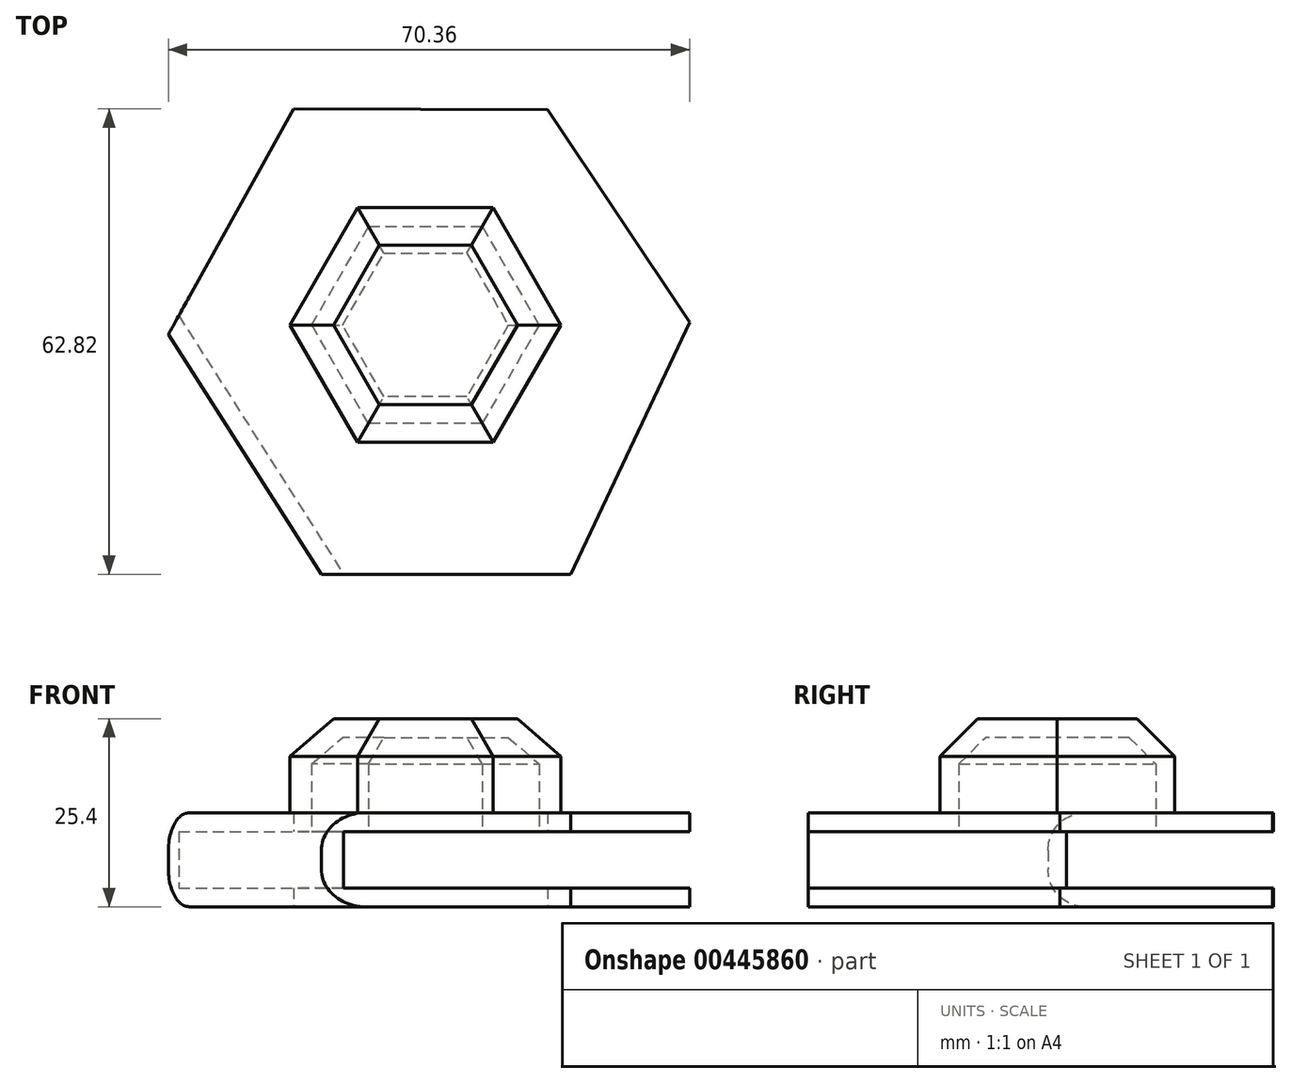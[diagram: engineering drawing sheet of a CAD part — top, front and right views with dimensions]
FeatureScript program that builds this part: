
annotation { "Feature Type Name" : "Feature", "Feature Type Description" : "" }
export const myFeature = defineFeature(function(context is Context, id is Id, definition is map)
    precondition{}
    {
        {
            var Q0;
            Q0=qCreatedBy(makeId("Top.planeOp"),FACE);
            var sketch = newSketch(context, id + "F0", { "sketchPlane" : qUnion([Q0])});
            skCircle(sketch, "E0.cCircle", {"center": v(-11.56, 13.08) * mm, "radius": 15.31 * mm, "construction": true});
            skLineSegment(sketch, "E0.0", {"start": v(-20.05, -2.43) * mm, "end": v(-29.24, 12.67) * mm});
            skLineSegment(sketch, "E0.1", {"start": v(-29.24, 12.67) * mm, "end": v(-20.76, 28.19) * mm});
            skLineSegment(sketch, "E0.2", {"start": v(-20.76, 28.19) * mm, "end": v(-3.08, 28.6) * mm});
            skLineSegment(sketch, "E0.3", {"start": v(-3.08, 28.6) * mm, "end": v(6.11, 13.5) * mm});
            skLineSegment(sketch, "E0.4", {"start": v(6.11, 13.5) * mm, "end": v(-2.37, -2.02) * mm});
            skLineSegment(sketch, "E0.5", {"start": v(-2.37, -2.02) * mm, "end": v(-20.05, -2.43) * mm});
            skPoint(sketch, "E0.0.midPoint", {"position": v(-24.65, 5.12) * mm});
            skLineSegment(sketch, "E1", {"start": v(-2.37, -2.02) * mm, "end": v(7.82, -20.12) * mm});
            skLineSegment(sketch, "E2", {"start": v(7.82, -20.12) * mm, "end": v(-25.85, -20.12) * mm});
            skLineSegment(sketch, "E3", {"start": v(-20.05, -2.43) * mm, "end": v(-25.85, -20.12) * mm});
            skLineSegment(sketch, "E4", {"start": v(6.11, 13.5) * mm, "end": v(23.86, 13.9) * mm});
            skLineSegment(sketch, "E5", {"start": v(23.86, 13.9) * mm, "end": v(7.82, -20.12) * mm});
            skPoint(sketch, "E6.endSnap0", {"position": v(1.52, 21.04) * mm});
            skLineSegment(sketch, "E7", {"start": v(-20.76, 28.19) * mm, "end": v(-29.6, 42.7) * mm});
            skLineSegment(sketch, "E8", {"start": v(-29.24, 12.67) * mm, "end": v(-46.5, 12.27) * mm});
            skLineSegment(sketch, "E9", {"start": v(-46.5, 12.27) * mm, "end": v(-29.6, 42.7) * mm});
            skLineSegment(sketch, "E10", {"start": v(-46.5, 12.27) * mm, "end": v(-25.85, -20.12) * mm});
            skPoint(sketch, "E11.end.orphan", {"position": v(1.52, 46.64) * mm});
            skLineSegment(sketch, "E12", {"start": v(-3.08, 28.6) * mm, "end": v(4.68, 42.57) * mm});
            skLineSegment(sketch, "E13", {"start": v(4.68, 42.57) * mm, "end": v(23.86, 13.9) * mm});
            skLineSegment(sketch, "E14", {"start": v(4.68, 42.57) * mm, "end": v(-29.6, 42.7) * mm});
            skSolve(sketch);
        }
        {
            var Q0;
            Q0=makeQuery(id+"F0.imprint","IMPRINT",FACE,{"disambiguationData":[TD([[makeQuery(id+"F0.imprint","IMPRINT",EDGE,{"derivedFrom":sQuery(id+"F0.wireOp",EDGE,"E0.2")}),1.0]])]});
            var Q1;
            Q1=makeQuery(id+"F0.imprint","IMPRINT",FACE,{"disambiguationData":[TD([[makeQuery(id+"F0.imprint","IMPRINT",EDGE,{"derivedFrom":sQuery(id+"F0.wireOp",EDGE,"E0.3")}),1.0]])]});
            var Q2;
            Q2=makeQuery(id+"F0.imprint","IMPRINT",FACE,{"disambiguationData":[TD([[makeQuery(id+"F0.imprint","IMPRINT",EDGE,{"derivedFrom":sQuery(id+"F0.wireOp",EDGE,"E0.4")}),1.0]])]});
            var Q3;
            Q3=makeQuery(id+"F0.imprint","IMPRINT",FACE,{"disambiguationData":[TD([[makeQuery(id+"F0.imprint","IMPRINT",EDGE,{"derivedFrom":sQuery(id+"F0.wireOp",EDGE,"E0.5")}),1.0]])]});
            var Q4;
            Q4=makeQuery(id+"F0.imprint","IMPRINT",FACE,{"disambiguationData":[TD([[makeQuery(id+"F0.imprint","IMPRINT",EDGE,{"derivedFrom":sQuery(id+"F0.wireOp",EDGE,"E0.0")}),1.0]])]});
            var Q5;
            Q5=makeQuery(id+"F0.imprint","IMPRINT",FACE,{"disambiguationData":[TD([[makeQuery(id+"F0.imprint","IMPRINT",EDGE,{"derivedFrom":sQuery(id+"F0.wireOp",EDGE,"E0.1")}),1.0]])]});
            var Q6;
            Q6=makeQuery(id+"F0.imprint","IMPRINT",FACE,{"disambiguationData":[TD([[makeQuery(id+"F0.imprint","IMPRINT",EDGE,{"derivedFrom":sQuery(id+"F0.wireOp",EDGE,"E0.0")}),-1.0]])]});
            extrude(context, id + "F1", {"entities" : qUnion([Q0, Q1, Q2, Q3, Q4, Q5, Q6]), "depth" : 12.7 * mm});
        }
        {
            var Q0;
            Q0=makeQuery(id+"F1.opExtrude","CAP_FACE",FACE,{"disambiguationData":[OSD([sQuery(id+"F0.wireOp",EDGE,"E2"),sQuery(id+"F0.wireOp",EDGE,"E5"),sQuery(id+"F0.wireOp",EDGE,"E9"),sQuery(id+"F0.wireOp",EDGE,"E10"),sQuery(id+"F0.wireOp",EDGE,"E13"),sQuery(id+"F0.wireOp",EDGE,"E14")])],"isStart":false});
            var sketch = newSketch(context, id + "F2", { "sketchPlane" : qUnion([Q0])});
            skCircle(sketch, "E15.cCircle", {"center": v(-11.8, 13.53) * mm, "radius": 15.83 * mm, "construction": true});
            skLineSegment(sketch, "E15.0", {"start": v(-2.66, -2.3) * mm, "end": v(-20.94, -2.3) * mm});
            skLineSegment(sketch, "E15.1", {"start": v(-20.94, -2.3) * mm, "end": v(-30.08, 13.53) * mm});
            skLineSegment(sketch, "E15.2", {"start": v(-30.08, 13.53) * mm, "end": v(-20.94, 29.36) * mm});
            skLineSegment(sketch, "E15.3", {"start": v(-20.94, 29.36) * mm, "end": v(-2.66, 29.36) * mm});
            skLineSegment(sketch, "E15.4", {"start": v(-2.66, 29.36) * mm, "end": v(6.48, 13.53) * mm});
            skLineSegment(sketch, "E15.5", {"start": v(6.48, 13.53) * mm, "end": v(-2.66, -2.3) * mm});
            skPoint(sketch, "E15.0.midPoint", {"position": v(-11.8, -2.3) * mm});
            skSolve(sketch);
        }
        {
            var Q0;
            Q0=makeQuery(id+"F2.imprint","IMPRINT",FACE,{"disambiguationData":[TD([[makeQuery(id+"F2.imprint","IMPRINT",EDGE,{"derivedFrom":sQuery(id+"F2.wireOp",EDGE,"E15.0")}),-1.0]])]});
            extrude(context, id + "F3", {"entities" : qUnion([Q0]), "operationType" : NewBodyOperationType.ADD, "depth" : 12.7 * mm});
        }
        {
            var Q0;
            Q0=makeQuery(id+"F3.opExtrude","CAP_EDGE",EDGE,{"disambiguationData":[OSD([sQuery(id+"F2.wireOp",EDGE,"E15.5")])],"isStart":false});
            var Q1;
            Q1=makeQuery(id+"F3.opExtrude","CAP_EDGE",EDGE,{"disambiguationData":[OSD([sQuery(id+"F2.wireOp",EDGE,"E15.4")])],"isStart":false});
            var Q2;
            Q2=makeQuery(id+"F3.opExtrude","CAP_EDGE",EDGE,{"disambiguationData":[OSD([sQuery(id+"F2.wireOp",EDGE,"E15.3")])],"isStart":false});
            var Q3;
            Q3=makeQuery(id+"F3.opExtrude","CAP_EDGE",EDGE,{"disambiguationData":[OSD([sQuery(id+"F2.wireOp",EDGE,"E15.2")])],"isStart":false});
            var Q4;
            Q4=makeQuery(id+"F3.opExtrude","CAP_EDGE",EDGE,{"disambiguationData":[OSD([sQuery(id+"F2.wireOp",EDGE,"E15.1")])],"isStart":false});
            var Q5;
            Q5=makeQuery(id+"F3.opExtrude","CAP_EDGE",EDGE,{"disambiguationData":[OSD([sQuery(id+"F2.wireOp",EDGE,"E15.0")])],"isStart":false});
            chamfer(context, id + "F4", {"entities" : qUnion([Q0, Q1, Q2, Q3, Q4, Q5]), "width" : 5.08 * mm, "tangentPropagation" : true});
        }
        {
            var Q0;
            Q0=makeQuery(id+"F1.opExtrude","SWEPT_FACE",FACE,{"disambiguationData":[OSD([sQuery(id+"F0.wireOp",EDGE,"E5")])]});
            var Q1;
            Q1=makeQuery(id+"F1.opExtrude","SWEPT_FACE",FACE,{"disambiguationData":[OSD([sQuery(id+"F0.wireOp",EDGE,"E2")])]});
            var Q2;
            Q2=makeQuery(id+"F1.opExtrude","SWEPT_FACE",FACE,{"disambiguationData":[OSD([sQuery(id+"F0.wireOp",EDGE,"E13")])]});
            var Q3;
            Q3=makeQuery(id+"F1.opExtrude","SWEPT_FACE",FACE,{"disambiguationData":[OSD([sQuery(id+"F0.wireOp",EDGE,"E14")])]});
            var Q4;
            Q4=makeQuery(id+"F1.opExtrude","SWEPT_FACE",FACE,{"disambiguationData":[OSD([sQuery(id+"F0.wireOp",EDGE,"E9")])]});
            shell(context, id + "F5", {"entities" : qUnion([Q0, Q1, Q2, Q3, Q4]), "thickness" : 2.54 * mm});
        }
        {
            var Q0;
            Q0=makeQuery(id+"F1.opExtrude","CAP_EDGE",EDGE,{"disambiguationData":[OSD([sQuery(id+"F0.wireOp",EDGE,"E10")])],"isStart":false});
            fillet(context, id + "F6", {"entities" : qUnion([Q0]), "radius" : 5.08 * mm, "tangentPropagation" : true, "allowEdgeOverflow" : false});
        }
        {
            var Q0;
            Q0=makeQuery(id+"F1.opExtrude","CAP_EDGE",EDGE,{"disambiguationData":[OSD([sQuery(id+"F0.wireOp",EDGE,"E10")])],"isStart":true});
            fillet(context, id + "F7", {"entities" : qUnion([Q0]), "radius" : 5.08 * mm, "tangentPropagation" : true, "allowEdgeOverflow" : false});
        }
    });
